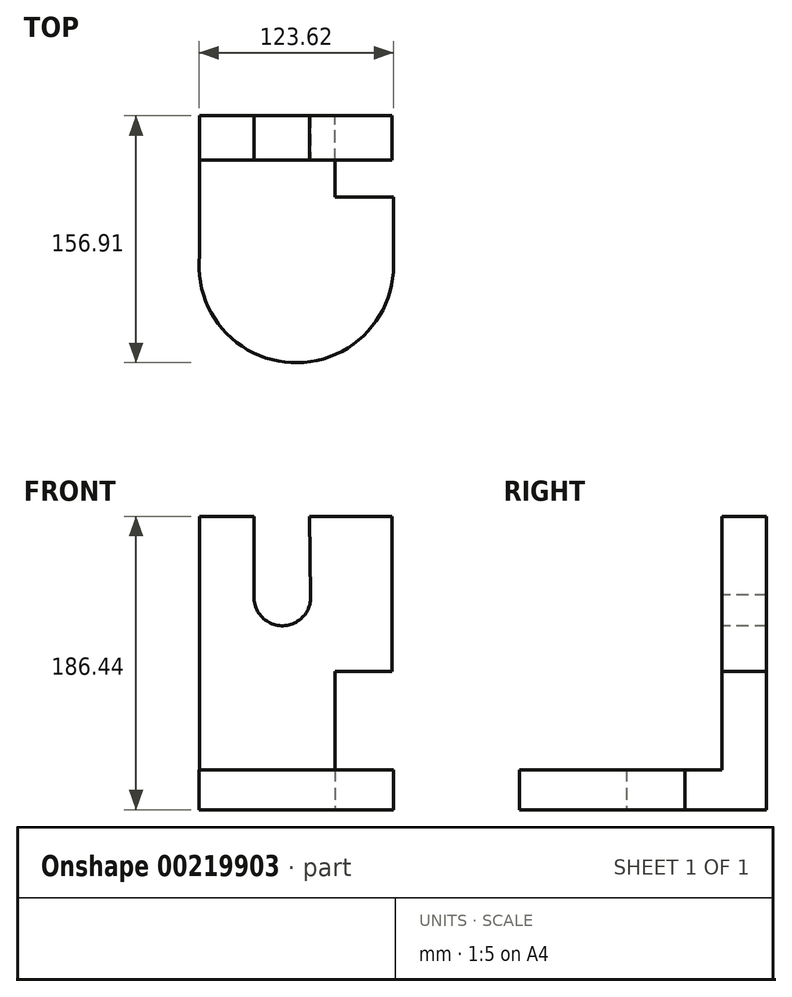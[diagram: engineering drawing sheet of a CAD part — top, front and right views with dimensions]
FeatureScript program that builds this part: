
annotation { "Feature Type Name" : "Feature", "Feature Type Description" : "" }
export const myFeature = defineFeature(function(context is Context, id is Id, definition is map)
    precondition{}
    {
        {
            var Q0;
            Q0=qCreatedBy(makeId("Top.planeOp"),FACE);
            var sketch = newSketch(context, id + "F0", { "sketchPlane" : qUnion([Q0])});
            skLineSegment(sketch, "E0.top", {"start": v(43.14, 25.86) * mm, "end": v(-43.14, 25.86) * mm});
            skLineSegment(sketch, "E0.left", {"start": v(43.14, -25.86) * mm, "end": v(43.14, 25.86) * mm});
            skLineSegment(sketch, "E0.right", {"start": v(-43.14, -25.86) * mm, "end": v(-43.14, 25.86) * mm});
            skPoint(sketch, "E0.middle", {"position": v(0, 0) * mm});
            skLineSegment(sketch, "E1.bottom", {"start": v(43.14, -25.86) * mm, "end": v(80.16, -25.86) * mm});
            skLineSegment(sketch, "E1.left", {"start": v(-43.14, -25.86) * mm, "end": v(-43.14, -62.98) * mm});
            skLineSegment(sketch, "E1.right", {"start": v(80.16, -25.86) * mm, "end": v(80.16, -69.24) * mm});
            skArc(sketch, "E2", {"start": v(-43.14, -62.98) * mm, "mid": v(15.21, -130.97) * mm, "end": v(80.16, -69.24) * mm});
            skSolve(sketch);
        }
        {
            var Q0;
            Q0 = qSketchRegion(id + "F0", true);
            extrude(context, id + "F1", {"entities" : qUnion([Q0]), "depth" : 25.4 * mm});
        }
        {
            var Q0;
            Q0=makeQuery(id+"F1.opExtrude","CAP_FACE",FACE,{"disambiguationData":[OSD([sQuery(id+"F0.wireOp",EDGE,"E0.top"),sQuery(id+"F0.wireOp",EDGE,"E0.left"),sQuery(id+"F0.wireOp",EDGE,"E0.right"),sQuery(id+"F0.wireOp",EDGE,"E1.bottom"),sQuery(id+"F0.wireOp",EDGE,"E1.left"),sQuery(id+"F0.wireOp",EDGE,"E1.right"),sQuery(id+"F0.wireOp",EDGE,"E2")])],"isStart":false});
            var sketch = newSketch(context, id + "F2", { "sketchPlane" : qUnion([Q0])});
            skLineSegment(sketch, "E3.bottom", {"start": v(-43.14, 25.86) * mm, "end": v(43.14, 25.86) * mm});
            skLineSegment(sketch, "E3.top", {"start": v(-43.14, -2.41) * mm, "end": v(43.14, -2.41) * mm});
            skLineSegment(sketch, "E3.left", {"start": v(-43.14, 25.86) * mm, "end": v(-43.14, -2.41) * mm});
            skLineSegment(sketch, "E3.right", {"start": v(43.14, 25.86) * mm, "end": v(43.14, -2.41) * mm});
            skSolve(sketch);
        }
        {
            var Q0;
            Q0 = qSketchRegion(id + "F2", true);
            extrude(context, id + "F3", {"entities" : qUnion([Q0]), "operationType" : NewBodyOperationType.ADD, "depth" : 161.04 * mm});
        }
        {
            var Q0;
            Q0=makeQuery(id+"F3.boolean.opBoolean","MERGE",FACE,{"derivedFrom":[makeQuery(id+"F1.opExtrude","SWEPT_FACE",FACE,{"disambiguationData":[OSD([sQuery(id+"F0.wireOp",EDGE,"E0.left")])]}),makeQuery(id+"F3.opExtrude","SWEPT_FACE",FACE,{"disambiguationData":[OSD([sQuery(id+"F2.wireOp",EDGE,"E3.right")])]})]});
            var sketch = newSketch(context, id + "F4", { "sketchPlane" : qUnion([Q0])});
            skLineSegment(sketch, "E4.bottom", {"start": v(-2.41, 186.44) * mm, "end": v(25.86, 186.44) * mm});
            skLineSegment(sketch, "E4.top", {"start": v(-2.41, 87.73) * mm, "end": v(25.86, 87.73) * mm});
            skLineSegment(sketch, "E4.left", {"start": v(-2.41, 186.44) * mm, "end": v(-2.41, 87.73) * mm});
            skLineSegment(sketch, "E4.right", {"start": v(25.86, 186.44) * mm, "end": v(25.86, 87.73) * mm});
            skSolve(sketch);
        }
        {
            var Q0;
            Q0 = qSketchRegion(id + "F4", true);
            extrude(context, id + "F5", {"entities" : qUnion([Q0]), "operationType" : NewBodyOperationType.ADD, "depth" : 36.07 * mm});
        }
        {
            var Q0;
            Q0=makeQuery(id+"F5.boolean.opBoolean","MERGE",FACE,{"derivedFrom":[makeQuery(id+"F3.opExtrude","SWEPT_FACE",FACE,{"disambiguationData":[OSD([sQuery(id+"F2.wireOp",EDGE,"E3.top")])]}),makeQuery(id+"F5.opExtrude","SWEPT_FACE",FACE,{"disambiguationData":[OSD([sQuery(id+"F4.wireOp",EDGE,"E4.left")])]})]});
            var sketch = newSketch(context, id + "F6", { "sketchPlane" : qUnion([Q0])});
            skCircle(sketch, "E5", {"center": v(9.54, 134.9) * mm, "radius": 18.02 * mm});
            skLineSegment(sketch, "E6", {"start": v(-8.4, 136.5) * mm, "end": v(-8.4, 186.44) * mm});
            skLineSegment(sketch, "E7", {"start": v(-8.4, 186.44) * mm, "end": v(26.65, 186.44) * mm});
            skLineSegment(sketch, "E8", {"start": v(26.65, 186.44) * mm, "end": v(27.56, 135.22) * mm});
            skSolve(sketch);
        }
        {
            var Q0;
            Q0 = qSketchRegion(id + "F6", true);
            extrude(context, id + "F7", {"entities" : qUnion([Q0]), "operationType" : NewBodyOperationType.REMOVE, "oppositeDirection" : true, "depth" : 66.55 * mm});
        }
    });
